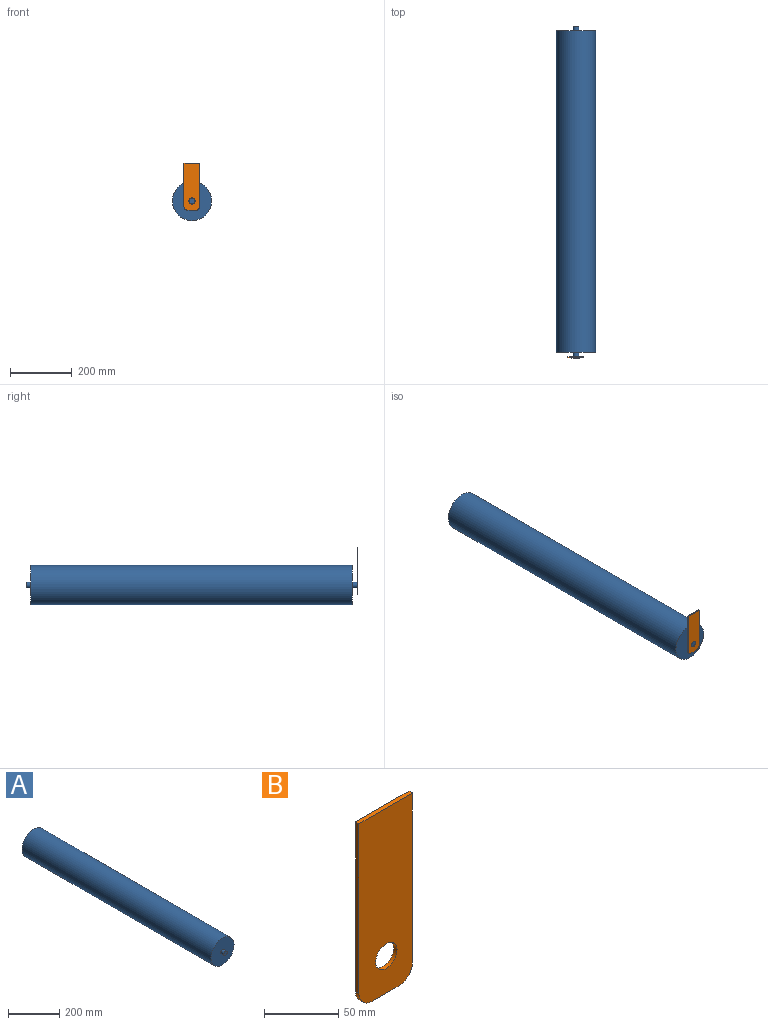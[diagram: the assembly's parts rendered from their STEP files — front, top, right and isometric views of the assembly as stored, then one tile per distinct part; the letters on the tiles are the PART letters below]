
ASSEMBLY  parts=2 mates=1
PART A: 7 faces, bbox 127x1073.4x127 mm
  f0: cylinder r=9.53mm len=19.05mm, axis (0,1,0), area 1003.3mm2, adj f1,f3
  f1: plane 19.05x19.05mm, normal (0,-1,0), area 285mm2, adj f0
  f2: cylinder r=63.5mm len=1041.4mm, axis (0,1,0), area 415500.1mm2, adj f3,f4
  f3: plane 127x127mm, normal (0,-1,0), area 12382.7mm2, adj f0,f2
  f4: plane 127x127mm, normal (0,1,0), area 12382.7mm2, adj f2,f6
  f5: plane 19.05x19.05mm, normal (0,1,0), area 285mm2, adj f6
  f6: cylinder r=9.53mm len=19.05mm, axis (0,1,0), area 912.1mm2, adj f4,f5
PART B: 9 faces, bbox 50.8x3.2x152.4 mm
  f0: plane 139.7x3.18mm, normal (-1,0,0), area 443.5mm2, adj f1,f5,f7,f8
  f1: cylinder r=12.7mm len=12.7mm, axis (0,1,0), area 63.3mm2, adj f0,f2,f7,f8
  f2: plane 25.4x3.18mm, normal (0,0,-1), area 80.6mm2, adj f1,f3,f7,f8
  f3: cylinder r=12.7mm len=12.7mm, axis (0,1,0), area 63.3mm2, adj f2,f4,f7,f8
  f4: plane 139.7x3.18mm, normal (1,0,0), area 443.5mm2, adj f3,f5,f7,f8
  f5: plane 50.8x3.18mm, normal (0,0,1), area 161.3mm2, adj f0,f4,f7,f8
  f6: cylinder r=10.16mm len=20.32mm, axis (0,1,0), area 202.7mm2, adj f7,f8
  f7: plane 152.4x50.8mm, normal (0,-1,0), area 7348.4mm2, adj f0,f1,f2,f3,f4,f5,f6
  f8: plane 152.4x50.8mm, normal (0,1,0), area 7348.4mm2, adj f0,f1,f2,f3,f4,f5,f6
PLACE A t=(-520.75,664.61,-156.97)mm
PLACE B t=(-389.57,-391.96,-124.87)mm
MATE revolute B.f6 <-> A.f0  axis (0,1,0) through (-520.75,-393.55,-156.97)mm
